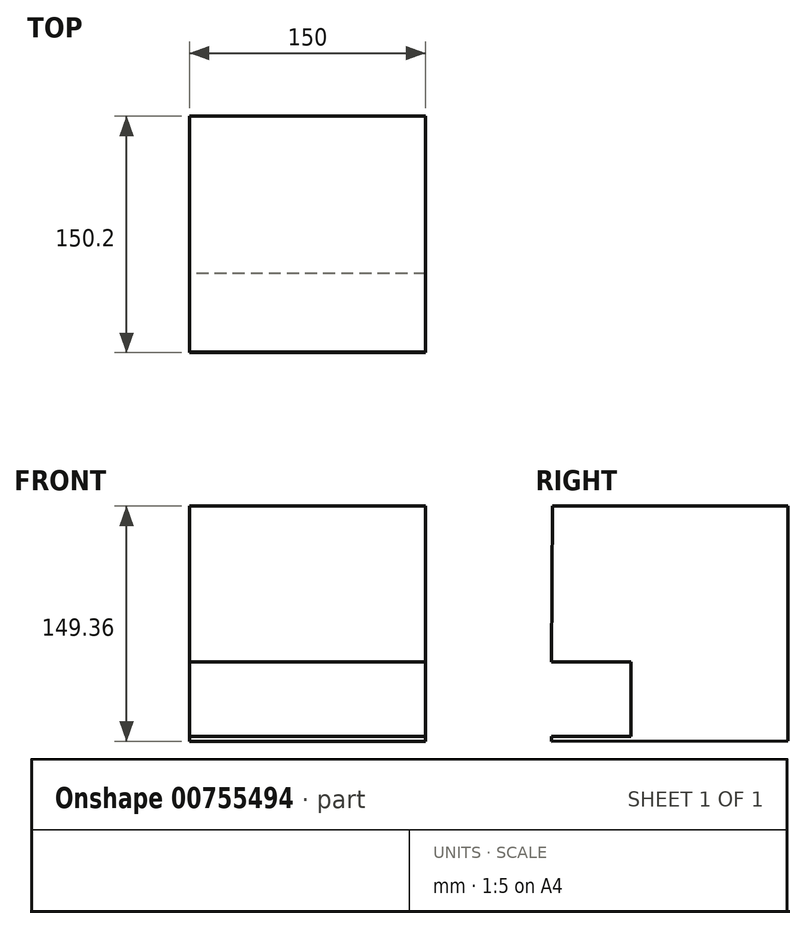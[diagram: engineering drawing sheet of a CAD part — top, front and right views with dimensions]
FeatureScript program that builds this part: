
annotation { "Feature Type Name" : "Feature", "Feature Type Description" : "" }
export const myFeature = defineFeature(function(context is Context, id is Id, definition is map)
    precondition{}
    {
        {
            var Q0;
            Q0=qCreatedBy(makeId("Right.planeOp"),FACE);
            var sketch = newSketch(context, id + "F0", { "sketchPlane" : qUnion([Q0])});
            skLineSegment(sketch, "E0", {"start": v(75.22, -74.54) * mm, "end": v(75.22, 74.57) * mm});
            skLineSegment(sketch, "E1", {"start": v(75.22, 74.57) * mm, "end": v(-74.54, 74.57) * mm});
            skLineSegment(sketch, "E2", {"start": v(-74.54, 74.57) * mm, "end": v(-74.97, -24.48) * mm});
            skLineSegment(sketch, "E3", {"start": v(-74.97, -24.48) * mm, "end": v(-24.69, -24.48) * mm});
            skLineSegment(sketch, "E4", {"start": v(-74.97, -74.79) * mm, "end": v(75.22, -74.54) * mm});
            skLineSegment(sketch, "E5", {"start": v(-74.97, -74.79) * mm, "end": v(-74.98, -71.79) * mm});
            skLineSegment(sketch, "E6", {"start": v(-74.98, -71.79) * mm, "end": v(-24.69, -71.7) * mm});
            skLineSegment(sketch, "E7", {"start": v(-24.69, -71.7) * mm, "end": v(-24.69, -24.48) * mm});
            skSolve(sketch);
        }
        {
            var Q0;
            Q0=makeQuery(id+"F0.imprint","IMPRINT",FACE,{"disambiguationData":[TD([[makeQuery(id+"F0.imprint","IMPRINT",EDGE,{"derivedFrom":sQuery(id+"F0.wireOp",EDGE,"E0")}),1.0]])]});
            extrude(context, id + "F1", {"entities" : qUnion([Q0]), "endBound" : BoundingType.SYMMETRIC, "depth" : 150 * mm, "offsetDistance" : 25 * mm});
        }
    });
